# Revit family: G6 vert. POE MS440219PM-48G6+
name_source: partatom
category: Datengeräte
units: mm (PartAtom-declared; Revit-internal decimal feet)

## family parameters
Arbeitsebenenbasiert = Nein
Beim Laden mit Abzugskörper schneiden = Nein
Bemaßung runder Anschluss = Durchmesser verwenden
Beschriftungsausrichtung beibehalten = Nein
Gemeinsam genutzt = Nein
Immer vertikal = Ja
OmniClass-Nummer = 23.85.50.17
OmniClass-Titel = Communication and Data Processing Equipment
Raumberechnungspunkt = Nein
Teiletyp = Normal

## types (1)
- G6 verti. PoE MS440209PM-48G6+
    Anschluss  4 = RS-232 Port (mini USB)
    Anschluss 1 = 1x 100/1000X SFP-Slot
    Anschluss 2 = 5x 10/100/1000T PoE+
    Anschluss 3 = microSD-Slot
    Anschluss 4 = 0 mm  [stored 0 ft]
    Artikelnummer = MS440219PM-48G6+
    Ausführung = vertikal
    Beschreibung = 6-Port GbE Micro Switch G6 PoE+
    Eigenschaft 1 = M45 Bauform
    Eigenschaft 2 = managed switch
    Hersteller = MICROSENS
    Spannung = 22..57 VDC
    Vorgabe-Ansicht = 0 mm  [stored 0 ft]

note: [stored X ft] marks values corroborated as IEEE doubles in the binary element streams (Revit-internal decimal feet)
